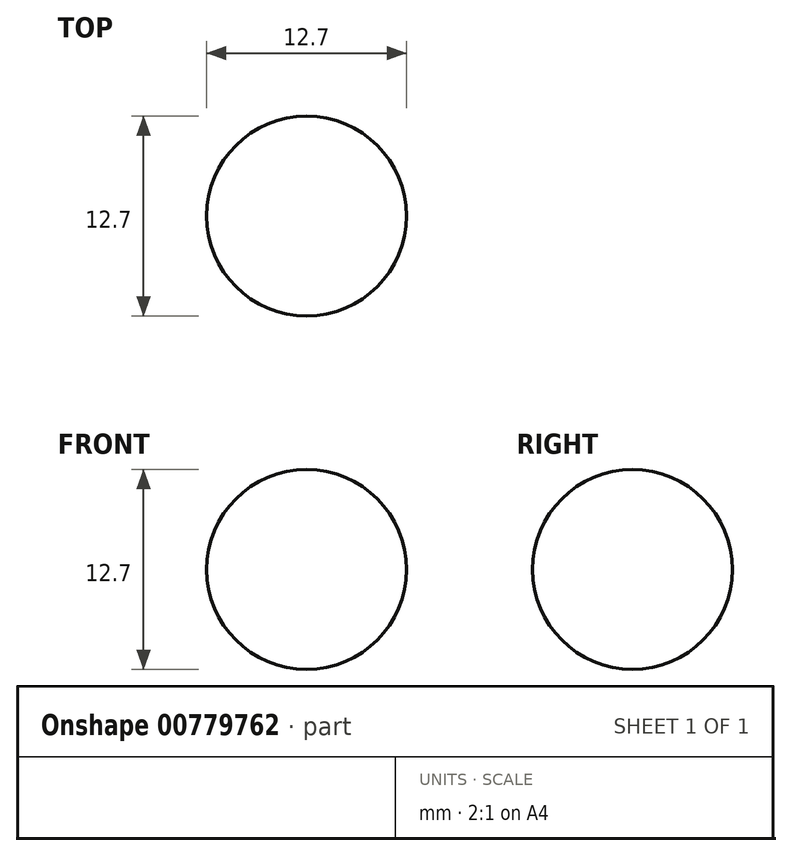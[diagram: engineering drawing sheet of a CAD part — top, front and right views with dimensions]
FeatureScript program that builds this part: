
annotation { "Feature Type Name" : "Feature", "Feature Type Description" : "" }
export const myFeature = defineFeature(function(context is Context, id is Id, definition is map)
    precondition{}
    {
        {
            var Q0;
            Q0=qCreatedBy(makeId("Top.planeOp"),FACE);
            var sketch = newSketch(context, id + "F0", { "sketchPlane" : qUnion([Q0])});
            skLineSegment(sketch, "E0", {"start": v(-10.35, 0) * mm, "end": v(8.72, 0) * mm});
            skArc(sketch, "E1", {"start": v(5.5, 0) * mm, "mid": v(-0.86, 6.35) * mm, "end": v(-7.2, 0) * mm});
            skSolve(sketch);
        }
        {
            var Q0;
            {var subQ0=sQuery(id+"F0.wireOp",EDGE,"E1");Q0=makeQuery(id+"F0.imprint","IMPRINT",FACE,{"disambiguationData":[TD([[makeQuery(id+"F0.imprint","IMPRINT",EDGE,{"derivedFrom":subQ0}),1.0]])]});}
            var Q1;
            Q1=sQuery(id+"F0.wireOp",EDGE,"E0");
            revolve(context, id + "F1", {"surfaceOperationType" : NewSurfaceOperationType.NEW, "entities" : qUnion([Q0]), "axis" : qUnion([Q1]), "revolveType" : RevolveType.FULL});
        }
    });
